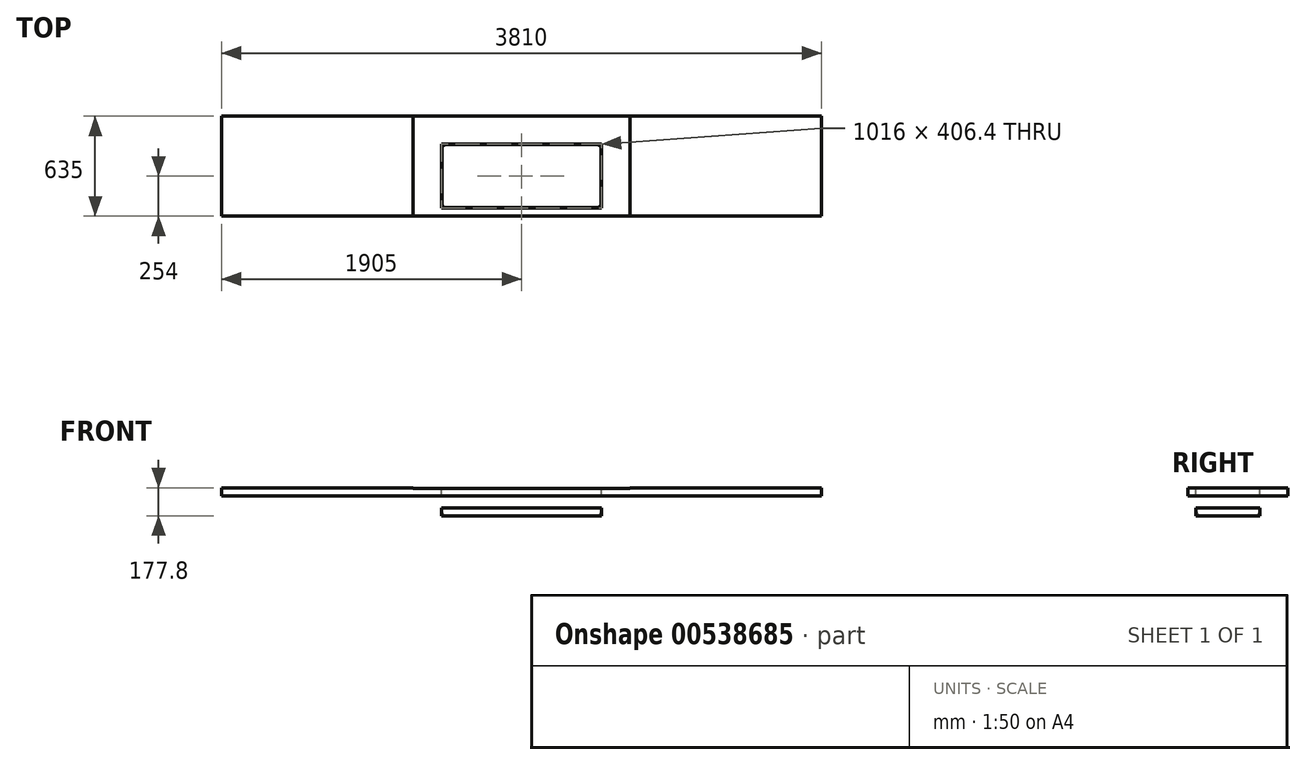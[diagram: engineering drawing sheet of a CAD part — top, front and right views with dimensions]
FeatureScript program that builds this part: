
annotation { "Feature Type Name" : "Feature", "Feature Type Description" : "" }
export const myFeature = defineFeature(function(context is Context, id is Id, definition is map)
    precondition{}
    {
        {
            var Q0;
            Q0=qCreatedBy(makeId("Top.planeOp"),FACE);
            var sketch = newSketch(context, id + "F0", { "sketchPlane" : qUnion([Q0])});
            skLineSegment(sketch, "E0.bottom", {"start": v(1905, -317.5) * mm, "end": v(-1905, -317.5) * mm});
            skLineSegment(sketch, "E0.top", {"start": v(1905, 317.5) * mm, "end": v(-1905, 317.5) * mm});
            skLineSegment(sketch, "E0.left", {"start": v(1905, -317.5) * mm, "end": v(1905, 317.5) * mm});
            skLineSegment(sketch, "E0.right", {"start": v(-1905, -317.5) * mm, "end": v(-1905, 317.5) * mm});
            skPoint(sketch, "E0.middle", {"position": v(0, 0) * mm});
            skSolve(sketch);
        }
        {
            var Q0;
            Q0=makeQuery(id+"F0.imprint","IMPRINT",FACE,{"disambiguationData":[TD([[makeQuery(id+"F0.imprint","IMPRINT",EDGE,{"derivedFrom":sQuery(id+"F0.wireOp",EDGE,"E0.bottom")}),-1.0]])]});
            extrude(context, id + "F1", {"entities" : qUnion([Q0]), "oppositeDirection" : true, "depth" : 50.8 * mm, "offsetDistance" : 25.4 * mm});
        }
        {
            var Q0;
            Q0=makeQuery(id+"F1.opExtrude","CAP_FACE",FACE,{"disambiguationData":[OSD([sQuery(id+"F0.wireOp",EDGE,"E0.bottom"),sQuery(id+"F0.wireOp",EDGE,"E0.top"),sQuery(id+"F0.wireOp",EDGE,"E0.left"),sQuery(id+"F0.wireOp",EDGE,"E0.right")])],"isStart":true});
            var sketch = newSketch(context, id + "F2", { "sketchPlane" : qUnion([Q0])});
            skLineSegment(sketch, "E1.bottom", {"start": v(508, -266.7) * mm, "end": v(-508, -266.7) * mm});
            skLineSegment(sketch, "E1.top", {"start": v(508, 139.7) * mm, "end": v(-508, 139.7) * mm});
            skLineSegment(sketch, "E1.left", {"start": v(508, -266.7) * mm, "end": v(508, 139.7) * mm});
            skLineSegment(sketch, "E1.right", {"start": v(-508, -266.7) * mm, "end": v(-508, 139.7) * mm});
            skPoint(sketch, "E1.middle", {"position": v(0, -63.5) * mm});
            skSolve(sketch);
        }
        {
            var Q0;
            Q0=makeQuery(id+"F2.imprint","IMPRINT",FACE,{"disambiguationData":[TD([[makeQuery(id+"F2.imprint","IMPRINT",EDGE,{"derivedFrom":sQuery(id+"F2.wireOp",EDGE,"E1.bottom")}),-1.0]])]});
            extrude(context, id + "F3", {"entities" : qUnion([Q0]), "oppositeDirection" : true, "depth" : 177.8 * mm, "offsetDistance" : 25.4 * mm});
        }
        {
            var Q0;
            Q0=makeQuery(id+"F3.opExtrude","CAP_FACE",FACE,{"disambiguationData":[OSD([sQuery(id+"F2.wireOp",EDGE,"E1.bottom"),sQuery(id+"F2.wireOp",EDGE,"E1.top"),sQuery(id+"F2.wireOp",EDGE,"E1.left"),sQuery(id+"F2.wireOp",EDGE,"E1.right")])],"isStart":true});
            var sketch = newSketch(context, id + "F4", { "sketchPlane" : qUnion([Q0])});
            skLineSegment(sketch, "E2.bottom", {"start": v(688.98, -317.5) * mm, "end": v(-688.98, -317.5) * mm});
            skLineSegment(sketch, "E2.top", {"start": v(688.98, 317.5) * mm, "end": v(-688.98, 317.5) * mm});
            skLineSegment(sketch, "E2.left", {"start": v(688.98, -317.5) * mm, "end": v(688.98, 317.5) * mm});
            skLineSegment(sketch, "E2.right", {"start": v(-688.98, -317.5) * mm, "end": v(-688.98, 317.5) * mm});
            skPoint(sketch, "E2.middle", {"position": v(0, 0) * mm});
            skSolve(sketch);
        }
        {
            var Q0;
            Q0=makeQuery(id+"F3.opExtrude","CAP_FACE",FACE,{"disambiguationData":[OSD([sQuery(id+"F2.wireOp",EDGE,"E1.bottom"),sQuery(id+"F2.wireOp",EDGE,"E1.top"),sQuery(id+"F2.wireOp",EDGE,"E1.left"),sQuery(id+"F2.wireOp",EDGE,"E1.right")])],"isStart":true});
            shell(context, id + "F5", {"entities" : qUnion([Q0]), "thickness" : 3.17 * mm});
        }
        {
            var Q0;
            Q0=makeQuery(id+"F4.imprint","IMPRINT",FACE,{"disambiguationData":[TD([[makeQuery(id+"F4.imprint","IMPRINT",EDGE,{"derivedFrom":sQuery(id+"F4.wireOp",EDGE,"E2.bottom")}),-1.0]])]});
            extrude(context, id + "F6", {"entities" : qUnion([Q0]), "operationType" : NewBodyOperationType.ADD, "oppositeDirection" : true, "depth" : 3.17 * mm, "offsetDistance" : 25.4 * mm});
        }
        {
            var Q0;
            Q0=makeQuery(id+"F4.imprint","IMPRINT",FACE,{"disambiguationData":[TD([[makeQuery(id+"F4.imprint","IMPRINT",EDGE,{"derivedFrom":sQuery(id+"F4.wireOp",EDGE,"E2.bottom")}),-1.0]])]});
            var Q1;
            Q1=makeQuery(id+"F4.imprint","IMPRINT",FACE,{"disambiguationData":[TD([[makeQuery(id+"F4.imprint","IMPRINT",EDGE,{"derivedFrom":makeQuery(id+"F3.opExtrude","CAP_EDGE",EDGE,{"disambiguationData":[OSD([sQuery(id+"F2.wireOp",EDGE,"E1.bottom")])],"isStart":true})}),-1.0]])]});
            extrude(context, id + "F7", {"entities" : qUnion([Q0, Q1]), "operationType" : NewBodyOperationType.REMOVE, "oppositeDirection" : true, "depth" : 3.17 * mm, "offsetDistance" : 25.4 * mm});
        }
        {
            var Q0;
            Q0=makeQuery(id+"F4.imprint","IMPRINT",FACE,{"disambiguationData":[TD([[makeQuery(id+"F4.imprint","IMPRINT",EDGE,{"derivedFrom":makeQuery(id+"F3.opExtrude","CAP_EDGE",EDGE,{"disambiguationData":[OSD([sQuery(id+"F2.wireOp",EDGE,"E1.bottom")])],"isStart":true})}),-1.0]])]});
            extrude(context, id + "F8", {"entities" : qUnion([Q0]), "operationType" : NewBodyOperationType.REMOVE, "oppositeDirection" : true, "depth" : 127 * mm, "offsetDistance" : 25.4 * mm});
        }
        {
            var Q0;
            Q0=makeQuery(id+"F5.opShell","OFFSET_EDGE",EDGE,{"disambiguationData":[OSD([sQuery(id+"F2.wireOp",EDGE,"E1.top"),sQuery(id+"F2.wireOp",EDGE,"E1.right")])]});
            var Q1;
            Q1=makeQuery(id+"F5.opShell","OFFSET_EDGE",EDGE,{"disambiguationData":[OSD([sQuery(id+"F2.wireOp",EDGE,"E1.top"),sQuery(id+"F2.wireOp",EDGE,"E1.left")])]});
            var Q2;
            Q2=makeQuery(id+"F5.opShell","OFFSET_EDGE",EDGE,{"disambiguationData":[OSD([sQuery(id+"F2.wireOp",EDGE,"E1.bottom"),sQuery(id+"F2.wireOp",EDGE,"E1.right")])]});
            var Q3;
            Q3=makeQuery(id+"F5.opShell","OFFSET_EDGE",EDGE,{"disambiguationData":[OSD([sQuery(id+"F2.wireOp",EDGE,"E1.bottom"),sQuery(id+"F2.wireOp",EDGE,"E1.left")])]});
            var Q4;
            Q4=makeQuery(id+"F5.opShell","OFFSET_FACE",FACE,{"disambiguationData":[OSD([sQuery(id+"F2.wireOp",EDGE,"E1.bottom"),sQuery(id+"F2.wireOp",EDGE,"E1.top"),sQuery(id+"F2.wireOp",EDGE,"E1.left"),sQuery(id+"F2.wireOp",EDGE,"E1.right")])]});
            fillet(context, id + "F9", {"entities" : qUnion([Q0, Q1, Q2, Q3, Q4]), "radius" : 25.4 * mm, "tangentPropagation" : true, "allowEdgeOverflow" : false});
        }
    });
